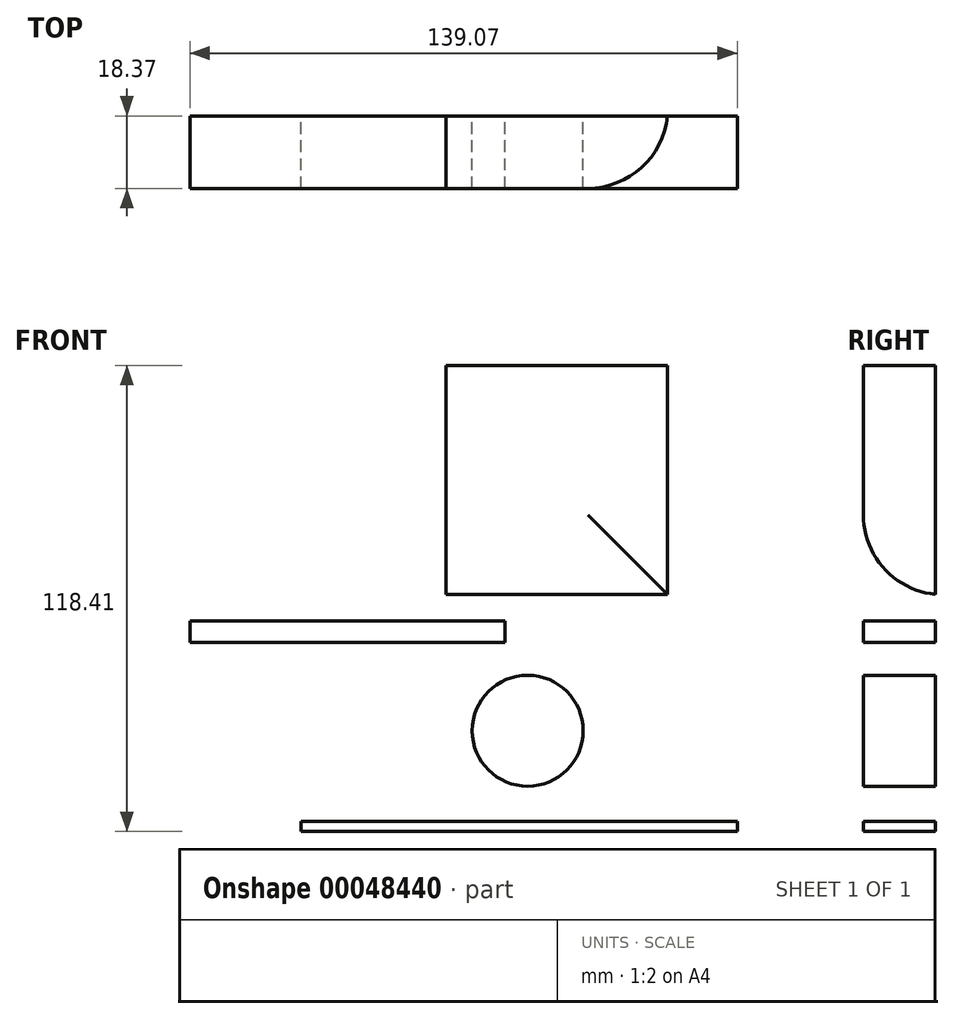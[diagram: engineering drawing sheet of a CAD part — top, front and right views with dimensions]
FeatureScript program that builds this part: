
annotation { "Feature Type Name" : "Feature", "Feature Type Description" : "" }
export const myFeature = defineFeature(function(context is Context, id is Id, definition is map)
    precondition{}
    {
        {
            var Q0;
            Q0=qCreatedBy(makeId("Front.planeOp"),FACE);
            var sketch = newSketch(context, id + "F0", { "sketchPlane" : qUnion([Q0])});
            skLineSegment(sketch, "E0", {"start": v(-45.68, 0) * mm, "end": v(71, 0) * mm});
            skLineSegment(sketch, "E1.bottom", {"start": v(-40.44, -50.33) * mm, "end": v(70.4, -50.33) * mm});
            skLineSegment(sketch, "E1.top", {"start": v(-40.44, -52.95) * mm, "end": v(70.4, -52.95) * mm});
            skLineSegment(sketch, "E1.left", {"start": v(-40.44, -50.33) * mm, "end": v(-40.44, -52.95) * mm});
            skLineSegment(sketch, "E1.right", {"start": v(70.4, -50.33) * mm, "end": v(70.4, -52.95) * mm});
            skLineSegment(sketch, "E2.rect.bottom", {"start": v(-3.65, 7.27) * mm, "end": v(52.66, 7.27) * mm});
            skLineSegment(sketch, "E2.rect.top", {"start": v(-3.65, 65.46) * mm, "end": v(52.66, 65.46) * mm});
            skLineSegment(sketch, "E2.rect.left", {"start": v(-3.65, 7.27) * mm, "end": v(-3.65, 65.46) * mm});
            skLineSegment(sketch, "E2.rect.right", {"start": v(52.66, 7.27) * mm, "end": v(52.66, 65.46) * mm});
            skPoint(sketch, "E2.rect.middle", {"position": v(24.5, 36.37) * mm});
            skCircle(sketch, "E3", {"center": v(17.17, -27.35) * mm, "radius": 14.1 * mm});
            skLineSegment(sketch, "E4.bottom", {"start": v(11.35, -4.95) * mm, "end": v(-68.66, -4.95) * mm});
            skLineSegment(sketch, "E4.top", {"start": v(11.35, 0.58) * mm, "end": v(-68.66, 0.58) * mm});
            skLineSegment(sketch, "E4.left", {"start": v(11.35, -4.95) * mm, "end": v(11.35, 0.58) * mm});
            skLineSegment(sketch, "E4.right", {"start": v(-68.66, -4.95) * mm, "end": v(-68.66, 0.58) * mm});
            skSolve(sketch);
        }
        {
            var Q0;
            Q0=makeQuery(id+"F0.imprint","IMPRINT",FACE,{"disambiguationData":[TD([[makeQuery(id+"F0.imprint","IMPRINT",EDGE,{"derivedFrom":sQuery(id+"F0.wireOp",EDGE,"E1.bottom")}),-1.0]])]});
            var Q1;
            Q1=makeQuery(id+"F0.imprint","IMPRINT",FACE,{"disambiguationData":[TD([[makeQuery(id+"F0.imprint","IMPRINT",EDGE,{"derivedFrom":sQuery(id+"F0.wireOp",EDGE,"E2.rect.bottom")}),1.0]])]});
            var Q2;
            Q2=makeQuery(id+"F0.imprint","IMPRINT",FACE,{"disambiguationData":[TD([[makeQuery(id+"F0.imprint","IMPRINT",EDGE,{"derivedFrom":sQuery(id+"F0.wireOp",EDGE,"E3")}),1.0]])]});
            var Q3;
            {var subQ2=sQuery(id+"F0.wireOp",EDGE,"E4.bottom");Q3=makeQuery(id+"F0.imprint","IMPRINT",FACE,{"disambiguationData":[TD([[makeQuery(id+"F0.imprint","IMPRINT",EDGE,{"derivedFrom":subQ2}),-1.0]])]});}
            extrude(context, id + "F1", {"entities" : qUnion([Q0, Q1, Q2, Q3]), "depth" : 18.37 * mm});
        }
        {
            var Q0;
            Q0=makeQuery(id+"F1.opExtrude","CAP_EDGE",EDGE,{"disambiguationData":[OSD([sQuery(id+"F0.wireOp",EDGE,"E2.rect.bottom")])],"isStart":false});
            fillet(context, id + "F2", {"entities" : qUnion([Q0]), "radius" : 20.32 * mm, "tangentPropagation" : true, "allowEdgeOverflow" : false});
        }
        {
            var Q0;
            Q0=makeQuery(id+"F1.opExtrude","CAP_EDGE",EDGE,{"disambiguationData":[OSD([sQuery(id+"F0.wireOp",EDGE,"E2.rect.right")])],"isStart":false});
            fillet(context, id + "F3", {"entities" : qUnion([Q0]), "radius" : 20.32 * mm, "tangentPropagation" : true, "allowEdgeOverflow" : false});
        }
    });
